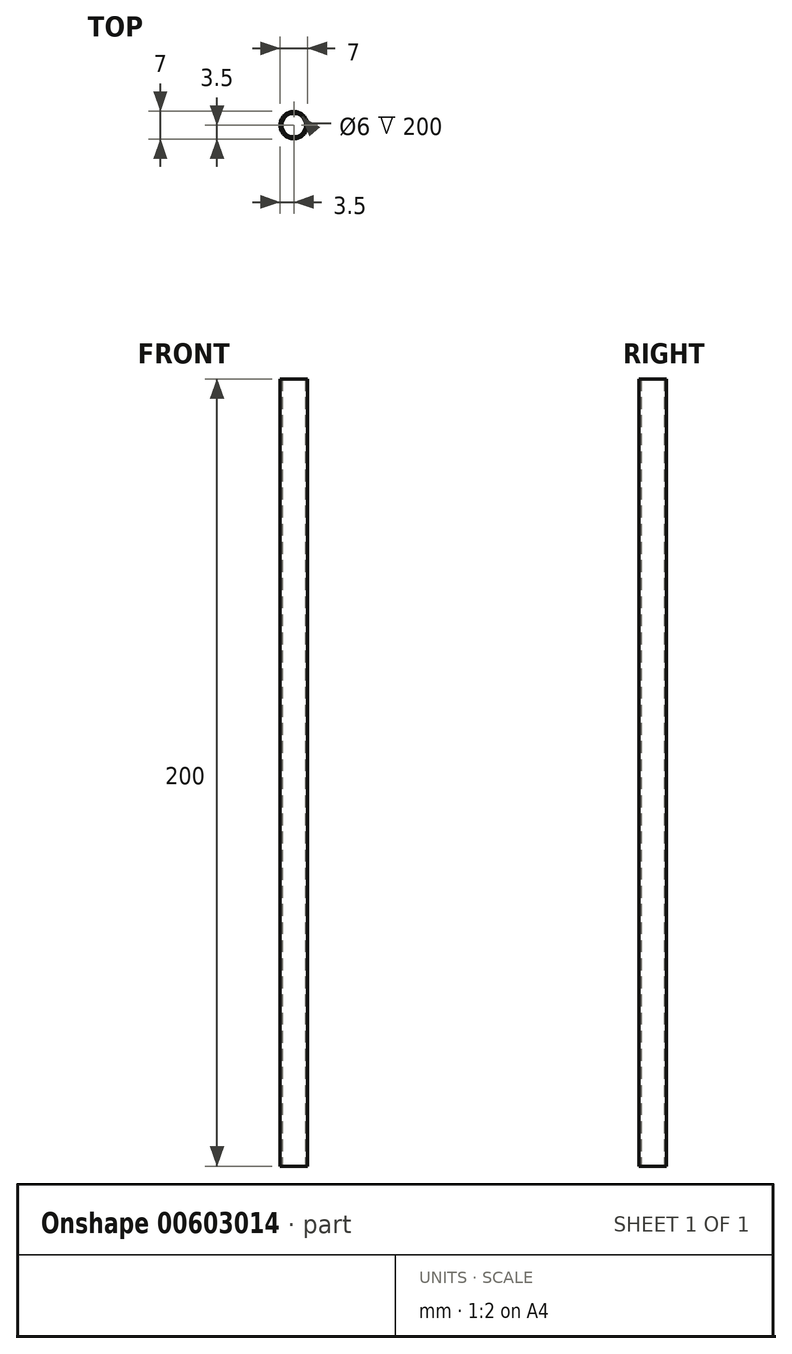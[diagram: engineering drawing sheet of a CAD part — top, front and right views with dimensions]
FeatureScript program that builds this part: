
annotation { "Feature Type Name" : "Feature", "Feature Type Description" : "" }
export const myFeature = defineFeature(function(context is Context, id is Id, definition is map)
    precondition{}
    {
        {
            var Q0;
            Q0=qCreatedBy(makeId("Front.planeOp"),FACE);
            var sketch = newSketch(context, id + "F0", { "sketchPlane" : qUnion([Q0])});
            skLineSegment(sketch, "E0", {"start": v(0, 0) * mm, "end": v(0, 205) * mm, "construction": true});
            skSolve(sketch);
        }
        {
            var Q0;
            Q0=qCreatedBy(makeId("Front.planeOp"),FACE);
            var sketch = newSketch(context, id + "F1", { "sketchPlane" : qUnion([Q0])});
            skLineSegment(sketch, "E1", {"start": v(-3.5, 0) * mm, "end": v(-3.5, 200) * mm});
            skLineSegment(sketch, "E2", {"start": v(-3, 0) * mm, "end": v(-3, 200) * mm});
            skPoint(sketch, "E2.endSnap0", {"position": v(-1.75, 200) * mm});
            skLineSegment(sketch, "E3", {"start": v(-3.5, 200) * mm, "end": v(-3, 200) * mm});
            skLineSegment(sketch, "E4", {"start": v(-3.5, 0) * mm, "end": v(-3, 0) * mm});
            skSolve(sketch);
        }
        {
            var Q0;
            Q0 = qSketchRegion(id + "F1", true);
            var Q1;
            Q1=sQuery(id+"F0.wireOp",EDGE,"E0");
            revolve(context, id + "F2", {"entities" : qUnion([Q0]), "axis" : qUnion([Q1]), "revolveType" : RevolveType.FULL});
        }
    });
